# Revit family: Tiefen_und_Plattener_Staberder_BP
name_source: partatom
category: Generic Models
revit_build: Autodesk Revit 2015 (Build: 20140606_1530(x64)
units: mm (PartAtom-declared; Revit-internal decimal feet)

## types (4) — shared parameters
Lenght 2 = 38 mm  [stored 0.124672 ft]
Manufacturer = OBO Bettermann
URL = http://www.obo-bettermann.com

## per-type parameters (varying)
| type | Article Type | Diameter dimesion | GTIN | Manufacturer Art. No. | Material | Outer Diameter Dimension |
| 219 25 BP FT | 219 25 BP FT | 13 mm | 4012195371953 | 5000955 | Steel, Galvanized | 8 mm  [stored 0.0262467 ft] |
| 219 20 BP FT | 219 20 BP FT | 10 mm  [stored 0.0328084 ft] | 4012195371892 | 50000947 | Steel, Galvanized | 6 mm  [stored 0.019685 ft] |
| 219 20 BP V4A(2) | 219 20 BP V4A | 10 mm  [stored 0.0328084 ft] | 4012195371830 | 50000866 | Stainless Steel AISI 304 | 6 mm  [stored 0.019685 ft] |
| 219 20 BP V4A | 219 20 BP V4A | 10 mm  [stored 0.0328084 ft] | 4012195740650 | 50000858 | Stainless Steel AISI 304 | 6 mm  [stored 0.019685 ft] |

note: [stored X ft] marks values corroborated as IEEE doubles in the binary element streams (Revit-internal decimal feet)

## geometry (parser evidence)
native form markers: Sweep x2
no freeform markers — native parametric forms only
